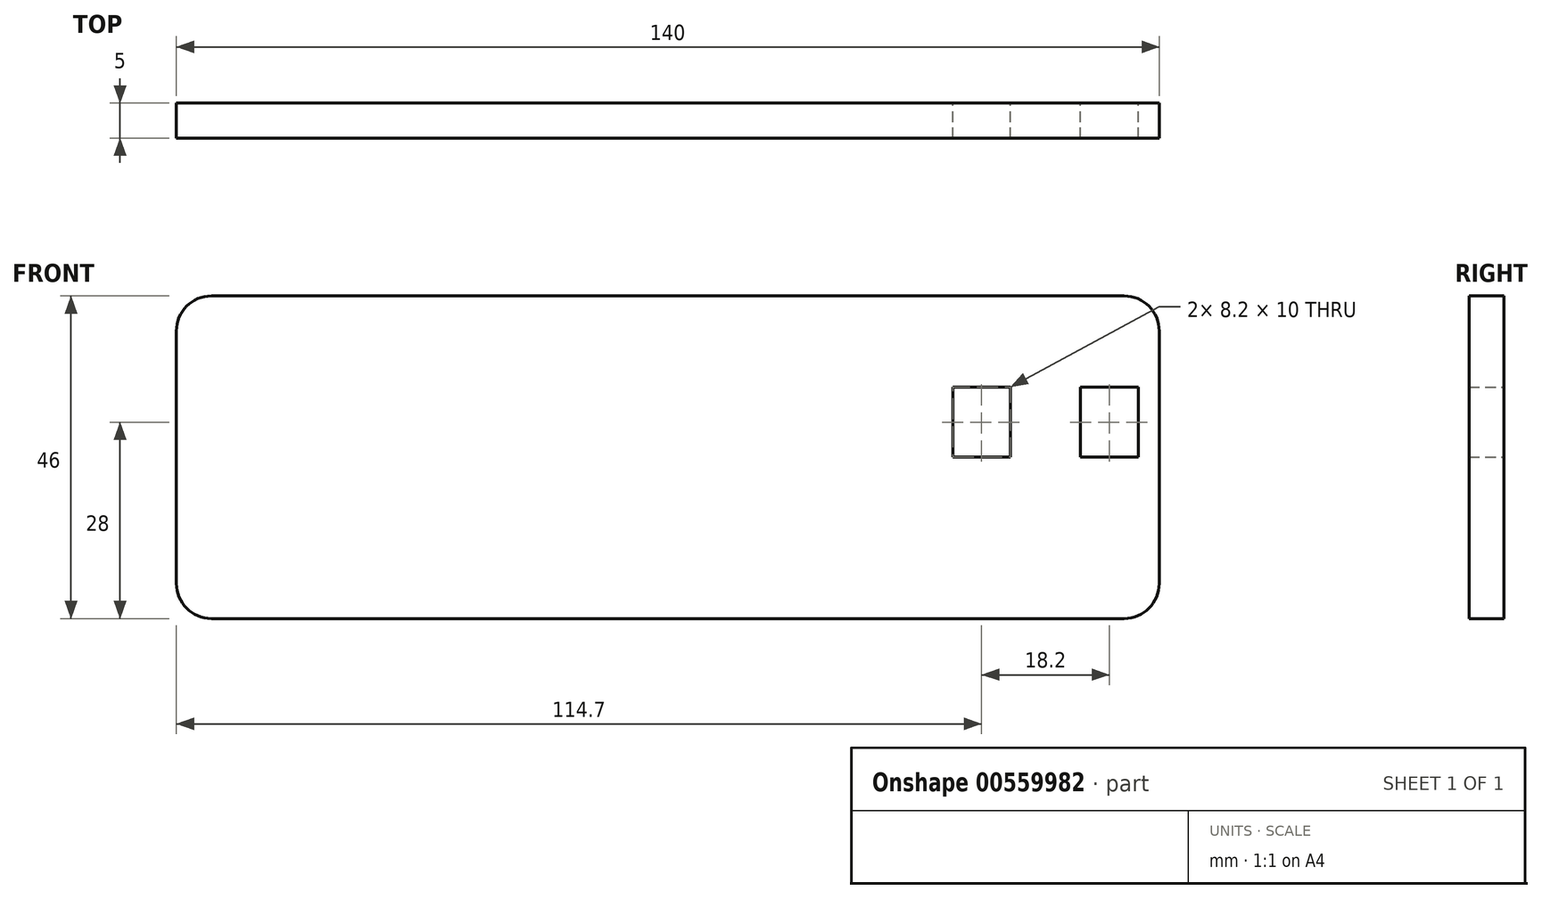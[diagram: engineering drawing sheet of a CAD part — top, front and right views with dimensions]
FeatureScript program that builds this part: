
annotation { "Feature Type Name" : "Feature", "Feature Type Description" : "" }
export const myFeature = defineFeature(function(context is Context, id is Id, definition is map)
    precondition{}
    {
        {
            var Q0;
            Q0=qCreatedBy(makeId("Front.planeOp"),FACE);
            var sketch = newSketch(context, id + "F0", { "sketchPlane" : qUnion([Q0])});
            skLineSegment(sketch, "E0.bottom", {"start": v(70, 23) * mm, "end": v(-70, 23) * mm});
            skLineSegment(sketch, "E0.top", {"start": v(70, -23) * mm, "end": v(-70, -23) * mm});
            skLineSegment(sketch, "E0.left", {"start": v(70, 23) * mm, "end": v(70, -23) * mm});
            skLineSegment(sketch, "E0.right", {"start": v(-70, 23) * mm, "end": v(-70, -23) * mm});
            skPoint(sketch, "E0.middle", {"position": v(0, 0) * mm});
            skLineSegment(sketch, "E1.bottom", {"start": v(70, 23) * mm, "end": v(25, 23) * mm});
            skLineSegment(sketch, "E1.top", {"start": v(70, -23) * mm, "end": v(25, -23) * mm});
            skLineSegment(sketch, "E1.right", {"start": v(25, 23) * mm, "end": v(25, -23) * mm});
            skPoint(sketch, "E1.middle", {"position": v(47.5, 0) * mm});
            skLineSegment(sketch, "E2.bottom", {"start": v(40.6, 10) * mm, "end": v(48.8, 10) * mm});
            skLineSegment(sketch, "E2.top", {"start": v(40.6, 0) * mm, "end": v(48.8, 0) * mm});
            skLineSegment(sketch, "E2.left", {"start": v(40.6, 10) * mm, "end": v(40.6, 0) * mm});
            skLineSegment(sketch, "E2.right", {"start": v(48.8, 10) * mm, "end": v(48.8, 0) * mm});
            skLineSegment(sketch, "E3.bottom", {"start": v(58.8, 10) * mm, "end": v(67, 10) * mm});
            skLineSegment(sketch, "E3.top", {"start": v(58.8, 0) * mm, "end": v(67, 0) * mm});
            skLineSegment(sketch, "E3.left", {"start": v(58.8, 10) * mm, "end": v(58.8, 0) * mm});
            skLineSegment(sketch, "E3.right", {"start": v(67, 10) * mm, "end": v(67, 0) * mm});
            skSolve(sketch);
        }
        {
            var Q0;
            Q0=qSketchRegion(id+"F0",true);
            extrude(context, id + "F1", {"entities" : qUnion([Q0]), "depth" : 10 * mm, "offsetDistance" : 25 * mm, "symmetric" : true});
        }
        {
            var Q0;
            Q0=qSketchRegion(id+"F0",true);
            extrude(context, id + "F2", {"entities" : qUnion([Q0]), "operationType" : NewBodyOperationType.REMOVE, "oppositeDirection" : true, "depth" : 25 * mm, "offsetDistance" : 25 * mm});
        }
        {
            var Q0;
            Q0=makeQuery(id+"F1.opExtrude","SWEPT_EDGE",EDGE,{"disambiguationData":[OSD([sQuery(id+"F0.wireOp",EDGE,"E0.bottom"),sQuery(id+"F0.wireOp",EDGE,"E0.right")])]});
            var Q1;
            Q1=makeQuery(id+"F1.opExtrude","SWEPT_EDGE",EDGE,{"disambiguationData":[OSD([sQuery(id+"F0.wireOp",EDGE,"E0.top"),sQuery(id+"F0.wireOp",EDGE,"E0.right")])]});
            var Q2;
            Q2=makeQuery(id+"F1.opExtrude","SWEPT_EDGE",EDGE,{"disambiguationData":[OSD([sQuery(id+"F0.wireOp",EDGE,"E1.bottom"),sQuery(id+"F0.wireOp",EDGE,"E0.left")])]});
            var Q3;
            Q3=makeQuery(id+"F1.opExtrude","SWEPT_EDGE",EDGE,{"disambiguationData":[OSD([sQuery(id+"F0.wireOp",EDGE,"E1.top"),sQuery(id+"F0.wireOp",EDGE,"E0.left")])]});
            fillet(context, id + "F3", {"entities" : qUnion([Q0, Q1, Q2, Q3]), "radius" : 5 * mm, "tangentPropagation" : true, "allowEdgeOverflow" : false});
        }
    });
